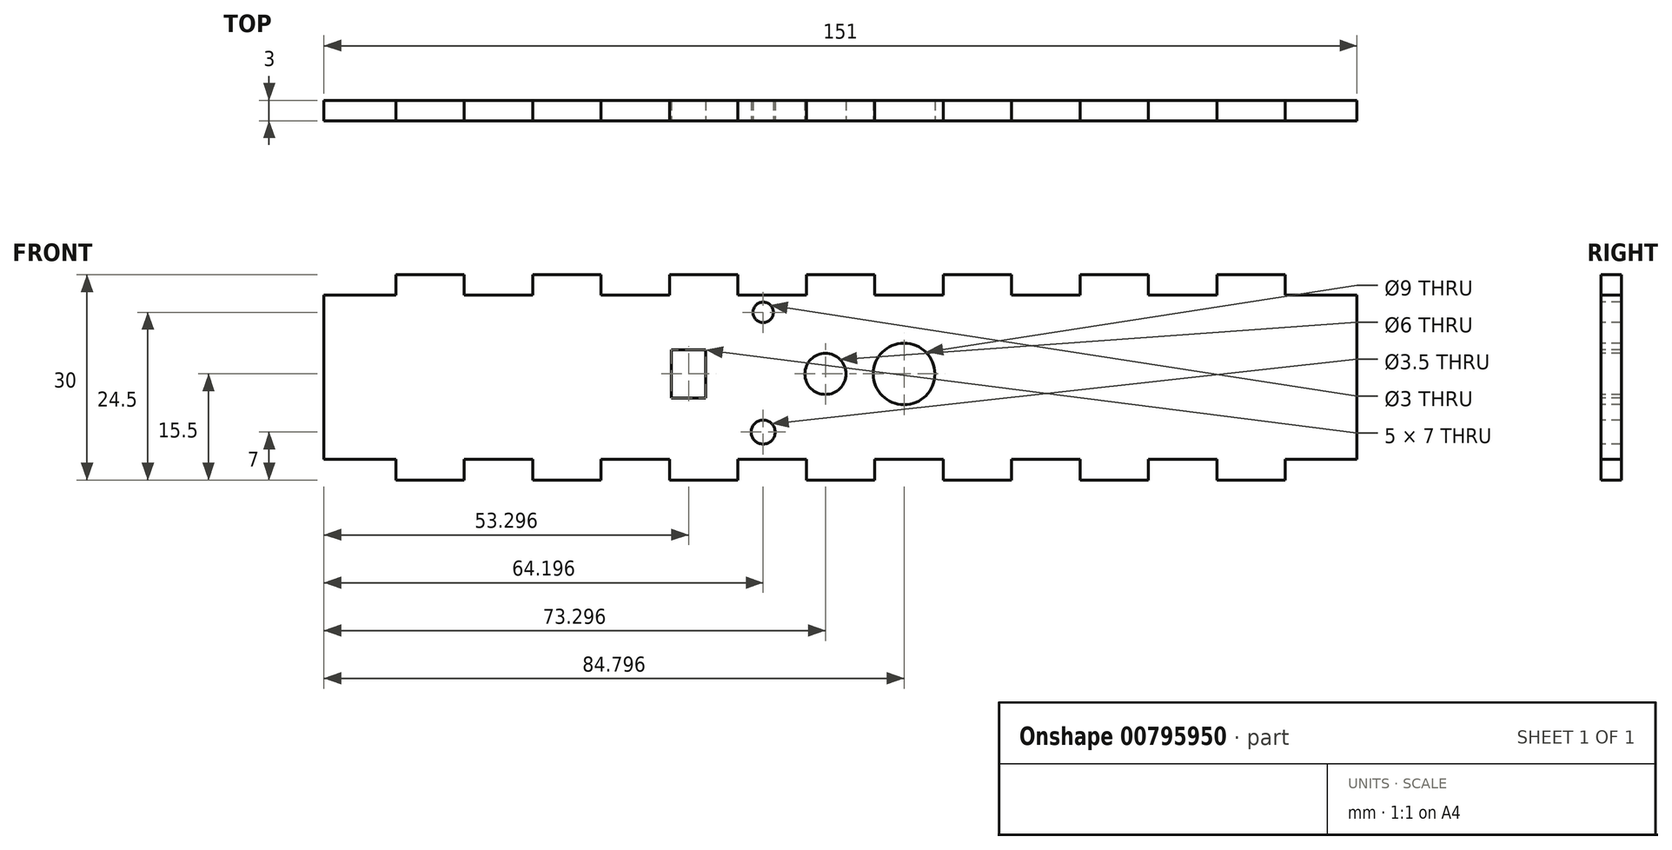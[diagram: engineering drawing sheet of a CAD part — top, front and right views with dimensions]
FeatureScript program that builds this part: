
annotation { "Feature Type Name" : "Feature", "Feature Type Description" : "" }
export const myFeature = defineFeature(function(context is Context, id is Id, definition is map)
    precondition{}
    {
        {
            var Q0;
            Q0=qCreatedBy(makeId("Front.planeOp"),FACE);
            var sketch = newSketch(context, id + "F0", { "sketchPlane" : qUnion([Q0])});
            skLineSegment(sketch, "E0.bottom", {"start": v(75.5, 15) * mm, "end": v(-75.5, 15) * mm});
            skLineSegment(sketch, "E0.top", {"start": v(75.5, -15) * mm, "end": v(-75.5, -15) * mm});
            skLineSegment(sketch, "E0.left", {"start": v(75.5, 15) * mm, "end": v(75.5, -15) * mm});
            skLineSegment(sketch, "E0.right", {"start": v(-75.5, 15) * mm, "end": v(-75.5, -15) * mm});
            skPoint(sketch, "E0.middle", {"position": v(0, 0) * mm});
            skSolve(sketch);
        }
        {
            var Q0;
            Q0=makeQuery(id+"F0.imprint","IMPRINT",FACE,{"disambiguationData":[TD([[makeQuery(id+"F0.imprint","IMPRINT",EDGE,{"derivedFrom":sQuery(id+"F0.wireOp",EDGE,"E0.bottom")}),1.0]])]});
            extrude(context, id + "F1", {"entities" : qUnion([Q0]), "depth" : 3 * mm, "offsetDistance" : 25 * mm});
        }
        {
            var Q0;
            Q0=makeQuery(id+"F1.opExtrude","CAP_FACE",FACE,{"disambiguationData":[OSD([sQuery(id+"F0.wireOp",EDGE,"E0.bottom"),sQuery(id+"F0.wireOp",EDGE,"E0.top"),sQuery(id+"F0.wireOp",EDGE,"E0.left"),sQuery(id+"F0.wireOp",EDGE,"E0.right")])],"isStart":false});
            var sketch = newSketch(context, id + "F2", { "sketchPlane" : qUnion([Q0])});
            skLineSegment(sketch, "E1.bottom", {"start": v(-75, -15) * mm, "end": v(-65, -15) * mm});
            skLineSegment(sketch, "E1.top", {"start": v(-75, -12) * mm, "end": v(-65, -12) * mm});
            skLineSegment(sketch, "E1.left", {"start": v(-75, -15) * mm, "end": v(-75, -12) * mm});
            skLineSegment(sketch, "E1.right", {"start": v(-65, -15) * mm, "end": v(-65, -12) * mm});
            skLineSegment(sketch, "E2.0.1.0", {"start": v(-75, 12) * mm, "end": v(-65, 12) * mm});
            skLineSegment(sketch, "E2.0.1.1", {"start": v(-75, 15) * mm, "end": v(-65, 15) * mm});
            skLineSegment(sketch, "E2.0.1.2", {"start": v(-75, 12) * mm, "end": v(-75, 15) * mm});
            skLineSegment(sketch, "E2.0.1.3", {"start": v(-65, 12) * mm, "end": v(-65, 15) * mm});
            skLineSegment(sketch, "E2.1.0.0", {"start": v(-55, -15) * mm, "end": v(-45, -15) * mm});
            skLineSegment(sketch, "E2.1.0.1", {"start": v(-55, -12) * mm, "end": v(-45, -12) * mm});
            skLineSegment(sketch, "E2.1.0.2", {"start": v(-55, -15) * mm, "end": v(-55, -12) * mm});
            skLineSegment(sketch, "E2.1.0.3", {"start": v(-45, -15) * mm, "end": v(-45, -12) * mm});
            skLineSegment(sketch, "E2.1.1.0", {"start": v(-55, 12) * mm, "end": v(-45, 12) * mm});
            skLineSegment(sketch, "E2.1.1.1", {"start": v(-55, 15) * mm, "end": v(-45, 15) * mm});
            skLineSegment(sketch, "E2.1.1.2", {"start": v(-55, 12) * mm, "end": v(-55, 15) * mm});
            skLineSegment(sketch, "E2.1.1.3", {"start": v(-45, 12) * mm, "end": v(-45, 15) * mm});
            skLineSegment(sketch, "E2.2.0.0", {"start": v(-35, -15) * mm, "end": v(-25, -15) * mm});
            skLineSegment(sketch, "E2.2.0.1", {"start": v(-35, -12) * mm, "end": v(-25, -12) * mm});
            skLineSegment(sketch, "E2.2.0.2", {"start": v(-35, -15) * mm, "end": v(-35, -12) * mm});
            skLineSegment(sketch, "E2.2.0.3", {"start": v(-25, -15) * mm, "end": v(-25, -12) * mm});
            skLineSegment(sketch, "E2.2.1.0", {"start": v(-35, 12) * mm, "end": v(-25, 12) * mm});
            skLineSegment(sketch, "E2.2.1.1", {"start": v(-35, 15) * mm, "end": v(-25, 15) * mm});
            skLineSegment(sketch, "E2.2.1.2", {"start": v(-35, 12) * mm, "end": v(-35, 15) * mm});
            skLineSegment(sketch, "E2.2.1.3", {"start": v(-25, 12) * mm, "end": v(-25, 15) * mm});
            skLineSegment(sketch, "E2.3.0.0", {"start": v(-15, -15) * mm, "end": v(-5, -15) * mm});
            skLineSegment(sketch, "E2.3.0.1", {"start": v(-15, -12) * mm, "end": v(-5, -12) * mm});
            skLineSegment(sketch, "E2.3.0.2", {"start": v(-15, -15) * mm, "end": v(-15, -12) * mm});
            skLineSegment(sketch, "E2.3.0.3", {"start": v(-5, -15) * mm, "end": v(-5, -12) * mm});
            skLineSegment(sketch, "E2.3.1.0", {"start": v(-15, 12) * mm, "end": v(-5, 12) * mm});
            skLineSegment(sketch, "E2.3.1.1", {"start": v(-15, 15) * mm, "end": v(-5, 15) * mm});
            skLineSegment(sketch, "E2.3.1.2", {"start": v(-15, 12) * mm, "end": v(-15, 15) * mm});
            skLineSegment(sketch, "E2.3.1.3", {"start": v(-5, 12) * mm, "end": v(-5, 15) * mm});
            skLineSegment(sketch, "E2.4.0.0", {"start": v(5, -15) * mm, "end": v(15, -15) * mm});
            skLineSegment(sketch, "E2.4.0.1", {"start": v(5, -12) * mm, "end": v(15, -12) * mm});
            skLineSegment(sketch, "E2.4.0.2", {"start": v(5, -15) * mm, "end": v(5, -12) * mm});
            skLineSegment(sketch, "E2.4.0.3", {"start": v(15, -15) * mm, "end": v(15, -12) * mm});
            skLineSegment(sketch, "E2.4.1.0", {"start": v(5, 12) * mm, "end": v(15, 12) * mm});
            skLineSegment(sketch, "E2.4.1.1", {"start": v(5, 15) * mm, "end": v(15, 15) * mm});
            skLineSegment(sketch, "E2.4.1.2", {"start": v(5, 12) * mm, "end": v(5, 15) * mm});
            skLineSegment(sketch, "E2.4.1.3", {"start": v(15, 12) * mm, "end": v(15, 15) * mm});
            skLineSegment(sketch, "E2.5.0.0", {"start": v(25, -15) * mm, "end": v(35, -15) * mm});
            skLineSegment(sketch, "E2.5.0.1", {"start": v(25, -12) * mm, "end": v(35, -12) * mm});
            skLineSegment(sketch, "E2.5.0.2", {"start": v(25, -15) * mm, "end": v(25, -12) * mm});
            skLineSegment(sketch, "E2.5.0.3", {"start": v(35, -15) * mm, "end": v(35, -12) * mm});
            skLineSegment(sketch, "E2.5.1.0", {"start": v(25, 12) * mm, "end": v(35, 12) * mm});
            skLineSegment(sketch, "E2.5.1.1", {"start": v(25, 15) * mm, "end": v(35, 15) * mm});
            skLineSegment(sketch, "E2.5.1.2", {"start": v(25, 12) * mm, "end": v(25, 15) * mm});
            skLineSegment(sketch, "E2.5.1.3", {"start": v(35, 12) * mm, "end": v(35, 15) * mm});
            skLineSegment(sketch, "E2.6.0.0", {"start": v(45, -15) * mm, "end": v(55, -15) * mm});
            skLineSegment(sketch, "E2.6.0.1", {"start": v(45, -12) * mm, "end": v(55, -12) * mm});
            skLineSegment(sketch, "E2.6.0.2", {"start": v(45, -15) * mm, "end": v(45, -12) * mm});
            skLineSegment(sketch, "E2.6.0.3", {"start": v(55, -15) * mm, "end": v(55, -12) * mm});
            skLineSegment(sketch, "E2.6.1.0", {"start": v(45, 12) * mm, "end": v(55, 12) * mm});
            skLineSegment(sketch, "E2.6.1.1", {"start": v(45, 15) * mm, "end": v(55, 15) * mm});
            skLineSegment(sketch, "E2.6.1.2", {"start": v(45, 12) * mm, "end": v(45, 15) * mm});
            skLineSegment(sketch, "E2.6.1.3", {"start": v(55, 12) * mm, "end": v(55, 15) * mm});
            skLineSegment(sketch, "E2.7.0.0", {"start": v(65, -15) * mm, "end": v(75, -15) * mm});
            skLineSegment(sketch, "E2.7.0.1", {"start": v(65, -12) * mm, "end": v(75, -12) * mm});
            skLineSegment(sketch, "E2.7.0.2", {"start": v(65, -15) * mm, "end": v(65, -12) * mm});
            skLineSegment(sketch, "E2.7.0.3", {"start": v(75, -15) * mm, "end": v(75, -12) * mm});
            skLineSegment(sketch, "E2.7.1.0", {"start": v(65, 12) * mm, "end": v(75, 12) * mm});
            skLineSegment(sketch, "E2.7.1.1", {"start": v(65, 15) * mm, "end": v(75, 15) * mm});
            skLineSegment(sketch, "E2.7.1.2", {"start": v(65, 12) * mm, "end": v(65, 15) * mm});
            skLineSegment(sketch, "E2.7.1.3", {"start": v(75, 12) * mm, "end": v(75, 15) * mm});
            skLineSegment(sketch, "E2.direction1", {"start": v(-75, -15) * mm, "end": v(-55, -15) * mm, "construction": true});
            skLineSegment(sketch, "E2.direction2", {"start": v(-75, -15) * mm, "end": v(-75, 12) * mm, "construction": true});
            skLineSegment(sketch, "E3.bottom", {"start": v(-70, 12) * mm, "end": v(-81.45, 12) * mm});
            skLineSegment(sketch, "E3.top", {"start": v(-70, 15) * mm, "end": v(-81.45, 15) * mm});
            skLineSegment(sketch, "E3.left", {"start": v(-70, 12) * mm, "end": v(-70, 15) * mm});
            skLineSegment(sketch, "E3.right", {"start": v(-81.45, 12) * mm, "end": v(-81.45, 15) * mm});
            skLineSegment(sketch, "E4.0.1.0", {"start": v(-70, -15) * mm, "end": v(-70, -12) * mm});
            skLineSegment(sketch, "E4.0.1.1", {"start": v(-81.45, -15) * mm, "end": v(-81.45, -12) * mm});
            skLineSegment(sketch, "E4.0.1.2", {"start": v(-70, -12) * mm, "end": v(-81.45, -12) * mm});
            skLineSegment(sketch, "E4.0.1.3", {"start": v(-70, -15) * mm, "end": v(-81.45, -15) * mm});
            skLineSegment(sketch, "E4.1.0.0", {"start": v(80, 12) * mm, "end": v(80, 15) * mm});
            skLineSegment(sketch, "E4.1.0.1", {"start": v(68.55, 12) * mm, "end": v(68.55, 15) * mm});
            skLineSegment(sketch, "E4.1.0.2", {"start": v(80, 15) * mm, "end": v(68.55, 15) * mm});
            skLineSegment(sketch, "E4.1.0.3", {"start": v(80, 12) * mm, "end": v(68.55, 12) * mm});
            skLineSegment(sketch, "E4.1.1.0", {"start": v(80, -15) * mm, "end": v(80, -12) * mm});
            skLineSegment(sketch, "E4.1.1.1", {"start": v(68.55, -15) * mm, "end": v(68.55, -12) * mm});
            skLineSegment(sketch, "E4.1.1.2", {"start": v(80, -12) * mm, "end": v(68.55, -12) * mm});
            skLineSegment(sketch, "E4.1.1.3", {"start": v(80, -15) * mm, "end": v(68.55, -15) * mm});
            skLineSegment(sketch, "E4.direction1", {"start": v(-81.45, 12) * mm, "end": v(68.55, 12) * mm, "construction": true});
            skLineSegment(sketch, "E4.direction2", {"start": v(-81.45, 12) * mm, "end": v(-81.45, -15) * mm, "construction": true});
            skCircle(sketch, "E5", {"center": v(9.3, 0.5) * mm, "radius": 4.5 * mm});
            skCircle(sketch, "E6", {"center": v(-11.3, 9.5) * mm, "radius": 1.5 * mm});
            skCircle(sketch, "E7", {"center": v(-11.3, -8) * mm, "radius": 1.75 * mm});
            skCircle(sketch, "E8", {"center": v(-2.2, 0.5) * mm, "radius": 3 * mm});
            skLineSegment(sketch, "E9.bottom", {"start": v(-24.7, -3) * mm, "end": v(-19.7, -3) * mm});
            skLineSegment(sketch, "E9.top", {"start": v(-24.7, 4) * mm, "end": v(-19.7, 4) * mm});
            skLineSegment(sketch, "E9.left", {"start": v(-24.7, -3) * mm, "end": v(-24.7, 4) * mm});
            skLineSegment(sketch, "E9.right", {"start": v(-19.7, -3) * mm, "end": v(-19.7, 4) * mm});
            skPoint(sketch, "E9.middle", {"position": v(-22.2, 0.5) * mm});
            skSolve(sketch);
        }
        {
            var Q0;
            Q0=qSketchRegion(id+"F2",true);
            extrude(context, id + "F3", {"entities" : qUnion([Q0]), "operationType" : NewBodyOperationType.REMOVE, "oppositeDirection" : true, "depth" : 25 * mm, "offsetDistance" : 25 * mm});
        }
    });
